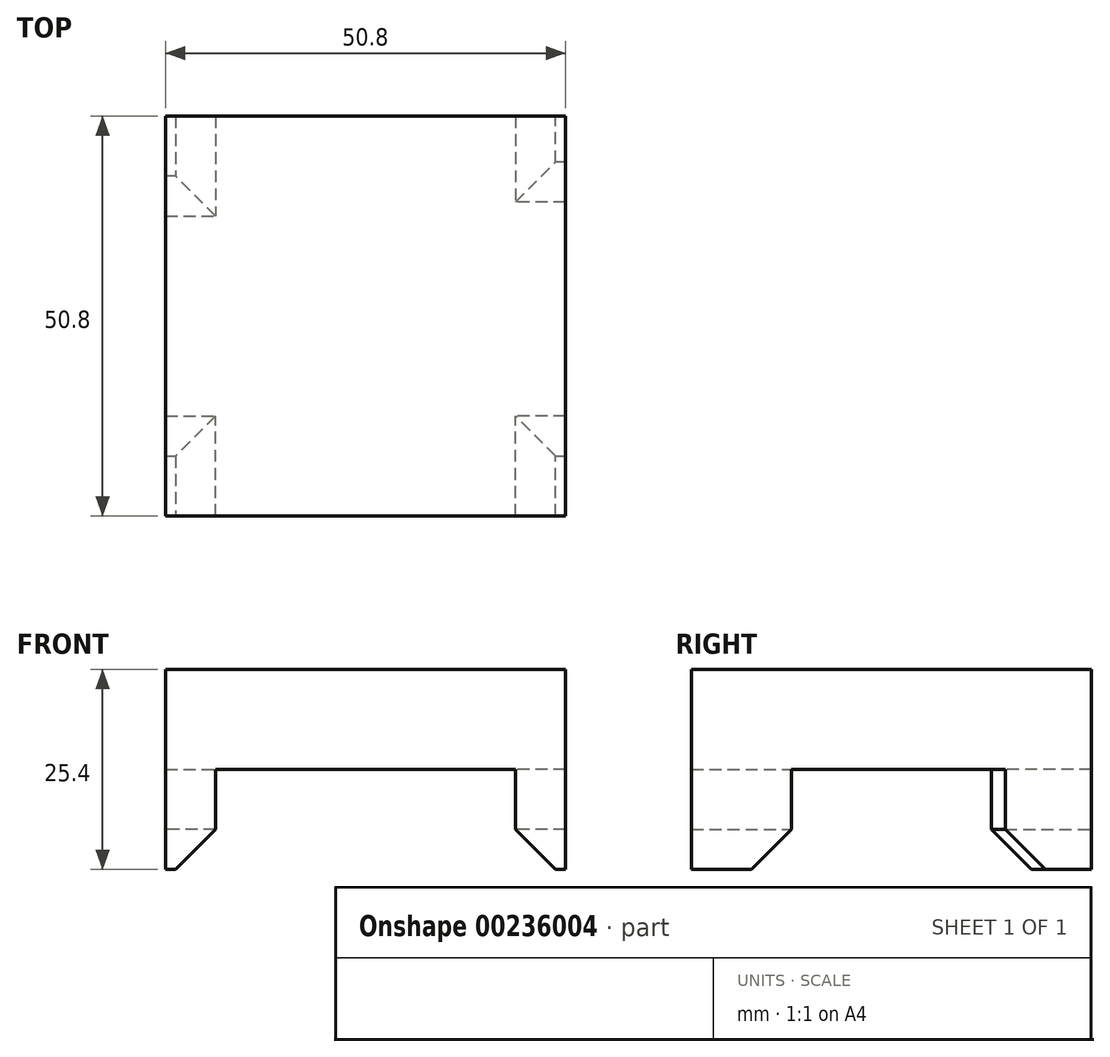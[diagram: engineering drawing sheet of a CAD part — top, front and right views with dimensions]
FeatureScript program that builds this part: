
annotation { "Feature Type Name" : "Feature", "Feature Type Description" : "" }
export const myFeature = defineFeature(function(context is Context, id is Id, definition is map)
    precondition{}
    {
        {
            var Q0;
            Q0=qCreatedBy(makeId("Top.planeOp"),FACE);
            var sketch = newSketch(context, id + "F0", { "sketchPlane" : qUnion([Q0])});
            skLineSegment(sketch, "E0.bottom", {"start": v(-24.63, -25.43) * mm, "end": v(26.17, -25.43) * mm});
            skLineSegment(sketch, "E0.top", {"start": v(-24.63, 25.37) * mm, "end": v(26.17, 25.37) * mm});
            skLineSegment(sketch, "E0.left", {"start": v(-24.63, -25.43) * mm, "end": v(-24.63, 25.37) * mm});
            skLineSegment(sketch, "E0.right", {"start": v(26.17, -25.43) * mm, "end": v(26.17, 25.37) * mm});
            skSolve(sketch);
        }
        {
            var Q0;
            Q0=qSketchRegion(id+"F0",true);
            extrude(context, id + "F1", {"entities" : qUnion([Q0]), "oppositeDirection" : true, "depth" : 12.7 * mm});
        }
        {
            var Q0;
            Q0=makeQuery(id+"F1.opExtrude","CAP_FACE",FACE,{"disambiguationData":[OSD([sQuery(id+"F0.wireOp",EDGE,"E0.bottom"),sQuery(id+"F0.wireOp",EDGE,"E0.top"),sQuery(id+"F0.wireOp",EDGE,"E0.left"),sQuery(id+"F0.wireOp",EDGE,"E0.right")])],"isStart":false});
            var sketch = newSketch(context, id + "F2", { "sketchPlane" : qUnion([Q0])});
            skLineSegment(sketch, "E1.bottom", {"start": v(-24.63, 25.43) * mm, "end": v(-18.28, 25.43) * mm});
            skLineSegment(sketch, "E1.top", {"start": v(-24.63, 12.73) * mm, "end": v(-18.28, 12.73) * mm});
            skLineSegment(sketch, "E1.left", {"start": v(-24.63, 25.43) * mm, "end": v(-24.63, 12.73) * mm});
            skLineSegment(sketch, "E1.right", {"start": v(-18.28, 25.43) * mm, "end": v(-18.28, 12.73) * mm});
            skLineSegment(sketch, "E2.bottom", {"start": v(26.17, 25.43) * mm, "end": v(19.82, 25.43) * mm});
            skLineSegment(sketch, "E2.top", {"start": v(26.17, 12.73) * mm, "end": v(19.82, 12.73) * mm});
            skLineSegment(sketch, "E2.left", {"start": v(26.17, 25.43) * mm, "end": v(26.17, 12.73) * mm});
            skLineSegment(sketch, "E2.right", {"start": v(19.82, 25.43) * mm, "end": v(19.82, 12.73) * mm});
            skLineSegment(sketch, "E3.bottom", {"start": v(-24.63, -25.37) * mm, "end": v(-18.28, -25.37) * mm});
            skLineSegment(sketch, "E3.top", {"start": v(-24.63, -12.67) * mm, "end": v(-18.28, -12.67) * mm});
            skLineSegment(sketch, "E3.left", {"start": v(-24.63, -25.37) * mm, "end": v(-24.63, -12.67) * mm});
            skLineSegment(sketch, "E3.right", {"start": v(-18.28, -25.37) * mm, "end": v(-18.28, -12.67) * mm});
            skLineSegment(sketch, "E4.bottom", {"start": v(26.17, -25.37) * mm, "end": v(19.82, -25.37) * mm});
            skLineSegment(sketch, "E4.top", {"start": v(26.17, -14.44) * mm, "end": v(19.82, -14.44) * mm});
            skLineSegment(sketch, "E4.left", {"start": v(26.17, -25.37) * mm, "end": v(26.17, -14.44) * mm});
            skLineSegment(sketch, "E4.right", {"start": v(19.82, -25.37) * mm, "end": v(19.82, -14.44) * mm});
            skSolve(sketch);
        }
        {
            var Q0;
            Q0=qSketchRegion(id+"F2",true);
            extrude(context, id + "F3", {"entities" : qUnion([Q0]), "operationType" : NewBodyOperationType.ADD, "depth" : 12.7 * mm});
        }
        {
            var Q0;
            Q0=makeQuery(id+"F3.opExtrude","CAP_EDGE",EDGE,{"disambiguationData":[OSD([sQuery(id+"F2.wireOp",EDGE,"E1.top")])],"isStart":false});
            var Q1;
            Q1=makeQuery(id+"F3.opExtrude","CAP_EDGE",EDGE,{"disambiguationData":[OSD([sQuery(id+"F2.wireOp",EDGE,"E1.right")])],"isStart":false});
            var Q2;
            Q2=makeQuery(id+"F3.opExtrude","CAP_EDGE",EDGE,{"disambiguationData":[OSD([sQuery(id+"F2.wireOp",EDGE,"E2.right")])],"isStart":false});
            var Q3;
            Q3=makeQuery(id+"F3.opExtrude","CAP_EDGE",EDGE,{"disambiguationData":[OSD([sQuery(id+"F2.wireOp",EDGE,"E2.top")])],"isStart":false});
            var Q4;
            Q4=makeQuery(id+"F3.opExtrude","CAP_EDGE",EDGE,{"disambiguationData":[OSD([sQuery(id+"F2.wireOp",EDGE,"E3.right")])],"isStart":false});
            var Q5;
            Q5=makeQuery(id+"F3.opExtrude","CAP_EDGE",EDGE,{"disambiguationData":[OSD([sQuery(id+"F2.wireOp",EDGE,"E3.top")])],"isStart":false});
            var Q6;
            Q6=makeQuery(id+"F3.opExtrude","CAP_EDGE",EDGE,{"disambiguationData":[OSD([sQuery(id+"F2.wireOp",EDGE,"E4.top")])],"isStart":false});
            var Q7;
            Q7=makeQuery(id+"F3.opExtrude","CAP_EDGE",EDGE,{"disambiguationData":[OSD([sQuery(id+"F2.wireOp",EDGE,"E4.right")])],"isStart":false});
            chamfer(context, id + "F4", {"entities" : qUnion([Q0, Q1, Q2, Q3, Q4, Q5, Q6, Q7]), "width" : 5.08 * mm, "tangentPropagation" : true});
        }
    });
